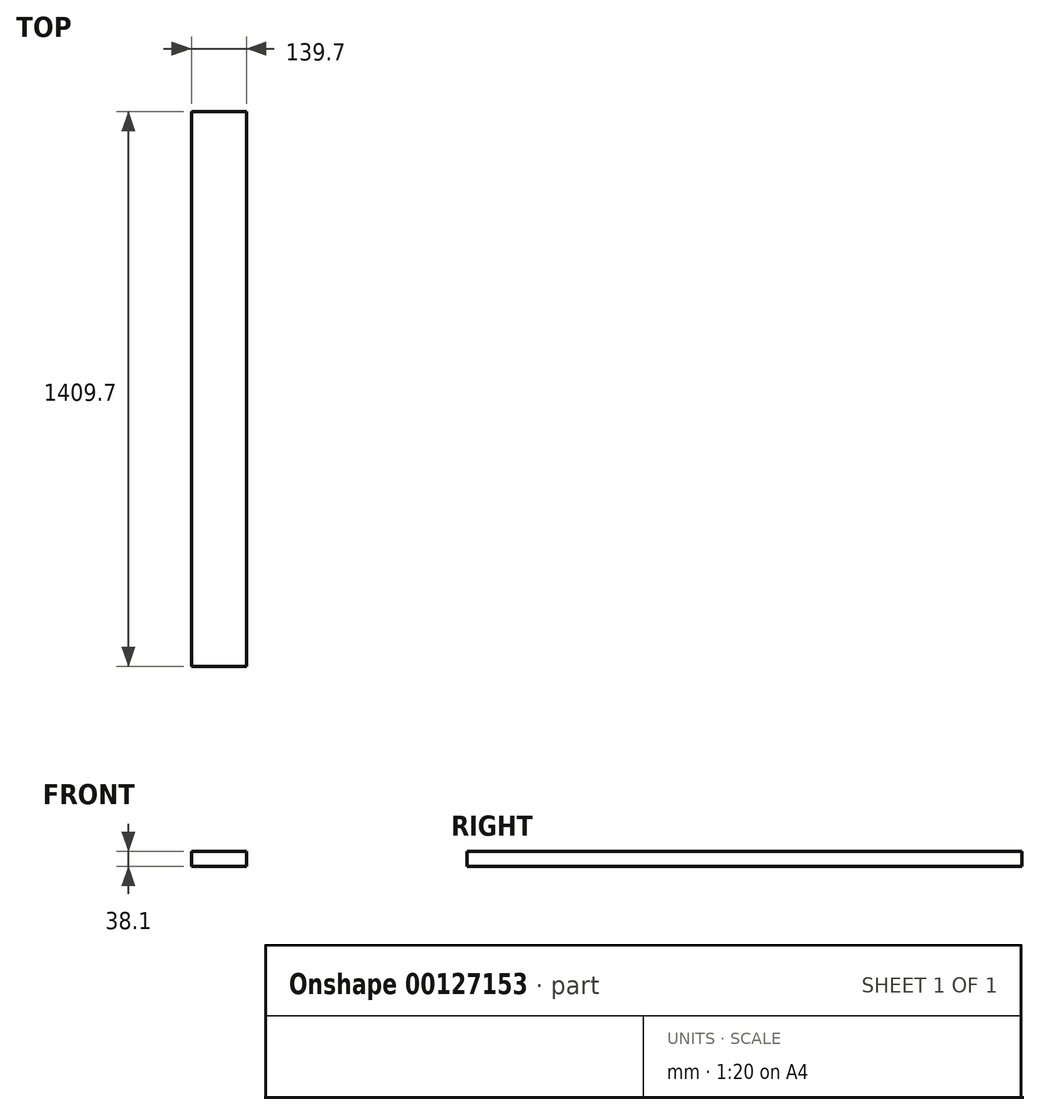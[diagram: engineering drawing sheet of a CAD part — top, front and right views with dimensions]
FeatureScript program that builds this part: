
annotation { "Feature Type Name" : "Feature", "Feature Type Description" : "" }
export const myFeature = defineFeature(function(context is Context, id is Id, definition is map)
    precondition{}
    {
        {
            var Q0;
            Q0=qCreatedBy(makeId("Front.planeOp"),FACE);
            var sketch = newSketch(context, id + "F0", { "sketchPlane" : qUnion([Q0])});
            skLineSegment(sketch, "E0.bottom", {"start": v(69.85, -19.05) * mm, "end": v(-69.85, -19.05) * mm});
            skLineSegment(sketch, "E0.top", {"start": v(69.85, 19.05) * mm, "end": v(-69.85, 19.05) * mm});
            skLineSegment(sketch, "E0.left", {"start": v(69.85, -19.05) * mm, "end": v(69.85, 19.05) * mm});
            skLineSegment(sketch, "E0.right", {"start": v(-69.85, -19.05) * mm, "end": v(-69.85, 19.05) * mm});
            skPoint(sketch, "E0.middle", {"position": v(0, 0) * mm});
            skSolve(sketch);
        }
        {
            var Q0;
            Q0=qSketchRegion(id+"F0",true);
            extrude(context, id + "F1", {"entities" : qUnion([Q0]), "depth" : 1409.7 * mm, "offsetDistance" : 25.4 * mm});
        }
    });
